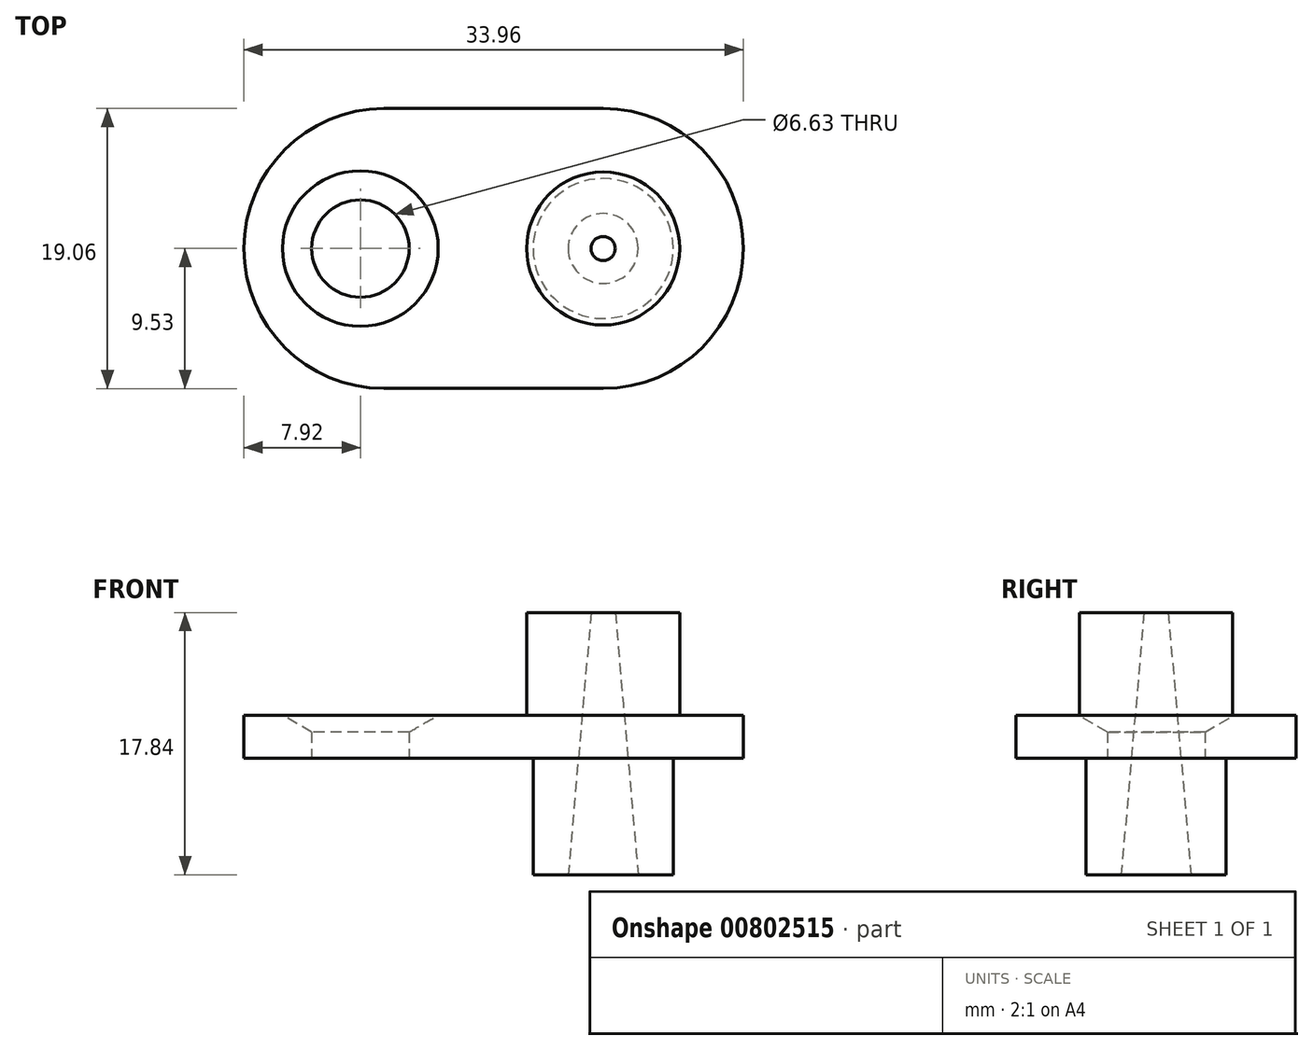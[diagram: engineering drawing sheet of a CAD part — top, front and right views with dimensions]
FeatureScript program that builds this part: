
annotation { "Feature Type Name" : "Feature", "Feature Type Description" : "" }
export const myFeature = defineFeature(function(context is Context, id is Id, definition is map)
    precondition{}
    {
        {
            var Q0;
            Q0=qCreatedBy(makeId("Top.planeOp"),FACE);
            var sketch = newSketch(context, id + "F0", { "sketchPlane" : qUnion([Q0])});
            skCircle(sketch, "E0", {"center": v(0, 0) * mm, "radius": 4.76 * mm});
            skSolve(sketch);
        }
        {
            var Q0;
            Q0 = qSketchRegion(id + "F0", true);
            extrude(context, id + "F1", {"entities" : qUnion([Q0]), "depth" : 7.94 * mm, "offsetDistance" : 25.4 * mm});
        }
        {
            var Q0;
            Q0=makeQuery(id+"F1.opExtrude","CAP_FACE",FACE,{"disambiguationData":[OSD([sQuery(id+"F0.wireOp",EDGE,"E0")])],"isStart":false});
            var sketch = newSketch(context, id + "F2", { "sketchPlane" : qUnion([Q0])});
            skArc(sketch, "E1", {"start": v(0, -9.53) * mm, "mid": v(9.53, 0) * mm, "end": v(0, 9.53) * mm});
            skArc(sketch, "E2", {"start": v(-14.9, 9.53) * mm, "mid": v(-24.43, 0) * mm, "end": v(-14.9, -9.53) * mm});
            skLineSegment(sketch, "E3", {"start": v(-14.9, 9.53) * mm, "end": v(0, 9.53) * mm});
            skLineSegment(sketch, "E4", {"start": v(-14.9, -9.53) * mm, "end": v(0, -9.53) * mm});
            skPoint(sketch, "E5", {"position": v(-24.43, 0) * mm});
            skPoint(sketch, "E6", {"position": v(9.53, 0) * mm});
            skPoint(sketch, "E7", {"position": v(4.76, 0) * mm});
            skCircle(sketch, "E8", {"center": v(-16.51, 0) * mm, "radius": 3.31 * mm});
            skSolve(sketch);
        }
        {
            var Q0;
            Q0 = qSketchRegion(id + "F2", true);
            extrude(context, id + "F3", {"entities" : qUnion([Q0]), "operationType" : NewBodyOperationType.ADD, "depth" : 2.92 * mm, "offsetDistance" : 25.4 * mm});
        }
        {
            var Q0;
            Q0=makeQuery(id+"F3.opExtrude","CAP_FACE",FACE,{"disambiguationData":[OSD([sQuery(id+"F2.wireOp",EDGE,"E1"),sQuery(id+"F2.wireOp",EDGE,"E2"),sQuery(id+"F2.wireOp",EDGE,"E3"),sQuery(id+"F2.wireOp",EDGE,"E4"),sQuery(id+"F2.wireOp",EDGE,"E8")])],"isStart":false});
            var sketch = newSketch(context, id + "F4", { "sketchPlane" : qUnion([Q0])});
            skCircle(sketch, "E9", {"center": v(0, 0) * mm, "radius": 5.2 * mm});
            skSolve(sketch);
        }
        {
            var Q0;
            Q0 = qSketchRegion(id + "F4", true);
            extrude(context, id + "F5", {"entities" : qUnion([Q0]), "operationType" : NewBodyOperationType.ADD, "depth" : 7 * mm, "offsetDistance" : 25.4 * mm});
        }
        {
            var Q0;
            Q0=makeQuery(id+"F3.opExtrude","CAP_EDGE",EDGE,{"disambiguationData":[OSD([sQuery(id+"F2.wireOp",EDGE,"E8")])],"isStart":false});
            chamfer(context, id + "F6", {"entities" : qUnion([Q0]), "chamferType" : ChamferType.OFFSET_ANGLE, "width" : 1.14 * mm, "oppositeDirection" : false, "angle" : 60 * degree, "tangentPropagation" : true});
        }
        {
            var Q0;
            Q0=makeQuery(id+"F1.opExtrude","CAP_FACE",FACE,{"disambiguationData":[OSD([sQuery(id+"F0.wireOp",EDGE,"E0")])],"isStart":true});
            var sketch = newSketch(context, id + "F7", { "sketchPlane" : qUnion([Q0])});
            skCircle(sketch, "E10", {"center": v(0, 0) * mm, "radius": 2.38 * mm});
            skSolve(sketch);
        }
        {
            var Q0;
            Q0 = qSketchRegion(id + "F7", true);
            extrude(context, id + "F8", {"entities" : qUnion([Q0]), "operationType" : NewBodyOperationType.REMOVE, "oppositeDirection" : true, "depth" : 25.4 * mm, "offsetDistance" : 25.4 * mm, "hasDraft" : true, "draftAngle" : 5 * degree, "draftPullDirection" : true});
        }
    });
